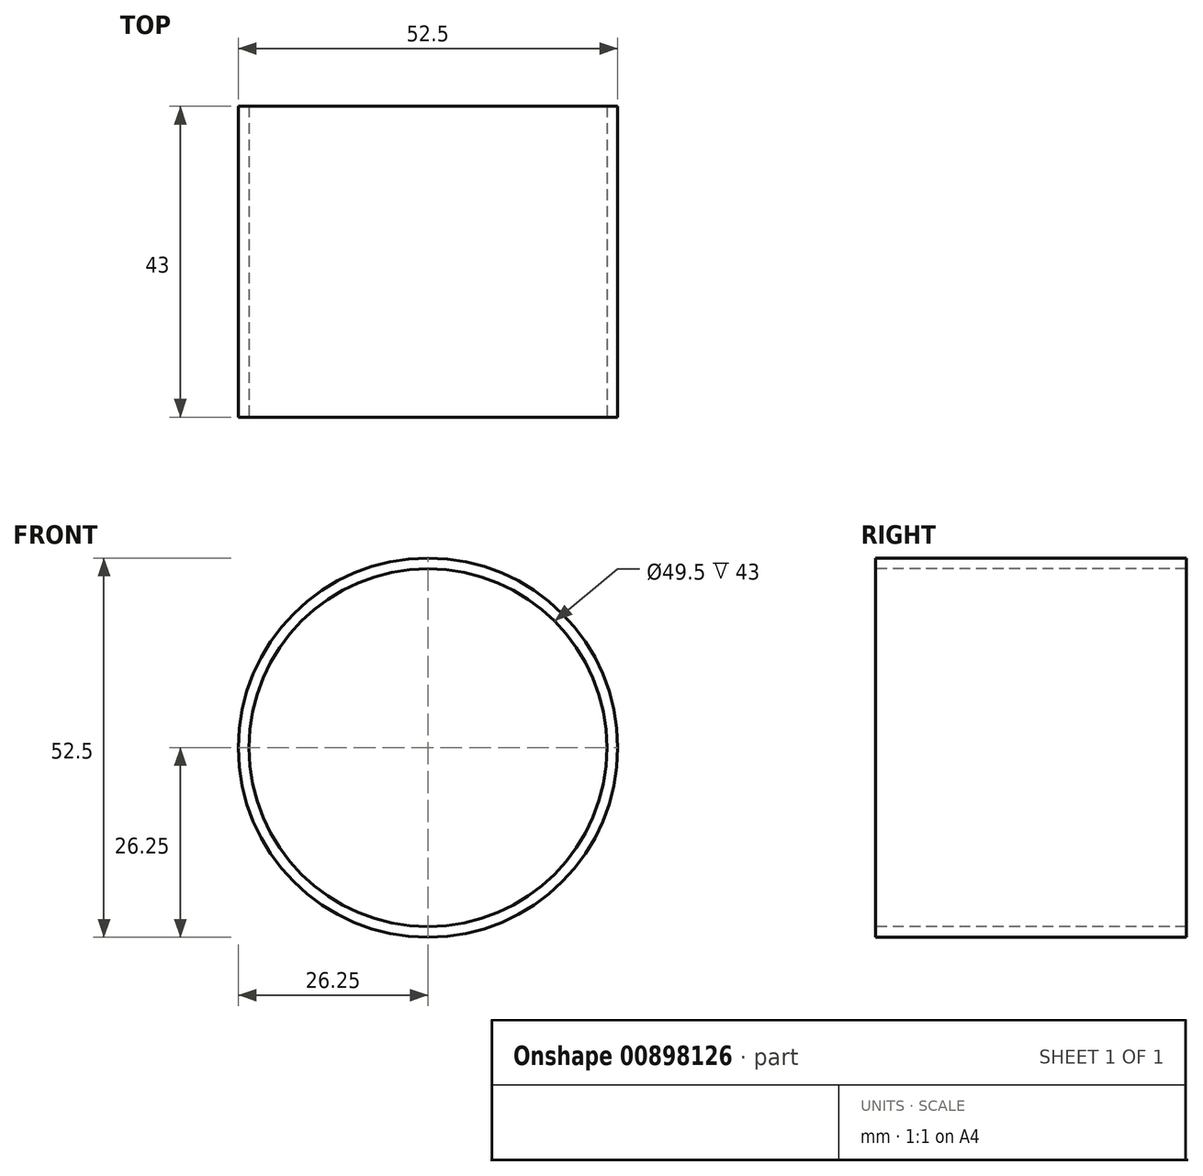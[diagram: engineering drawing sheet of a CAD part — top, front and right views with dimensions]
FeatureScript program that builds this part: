
annotation { "Feature Type Name" : "Feature", "Feature Type Description" : "" }
export const myFeature = defineFeature(function(context is Context, id is Id, definition is map)
    precondition{}
    {
        {
            var Q0;
            Q0=qCreatedBy(makeId("Front.planeOp"),FACE);
            var sketch = newSketch(context, id + "F0", { "sketchPlane" : qUnion([Q0])});
            skCircle(sketch, "E0", {"center": v(0, 0) * mm, "radius": 26.25 * mm});
            skCircle(sketch, "E1", {"center": v(0, 0) * mm, "radius": 24.75 * mm});
            skSolve(sketch);
        }
        {
            var Q0;
            Q0 = qSketchRegion(id + "F0", true);
            extrude(context, id + "F1", {"entities" : qUnion([Q0]), "oppositeDirection" : true, "depth" : 43 * mm, "offsetDistance" : 25 * mm});
        }
    });
